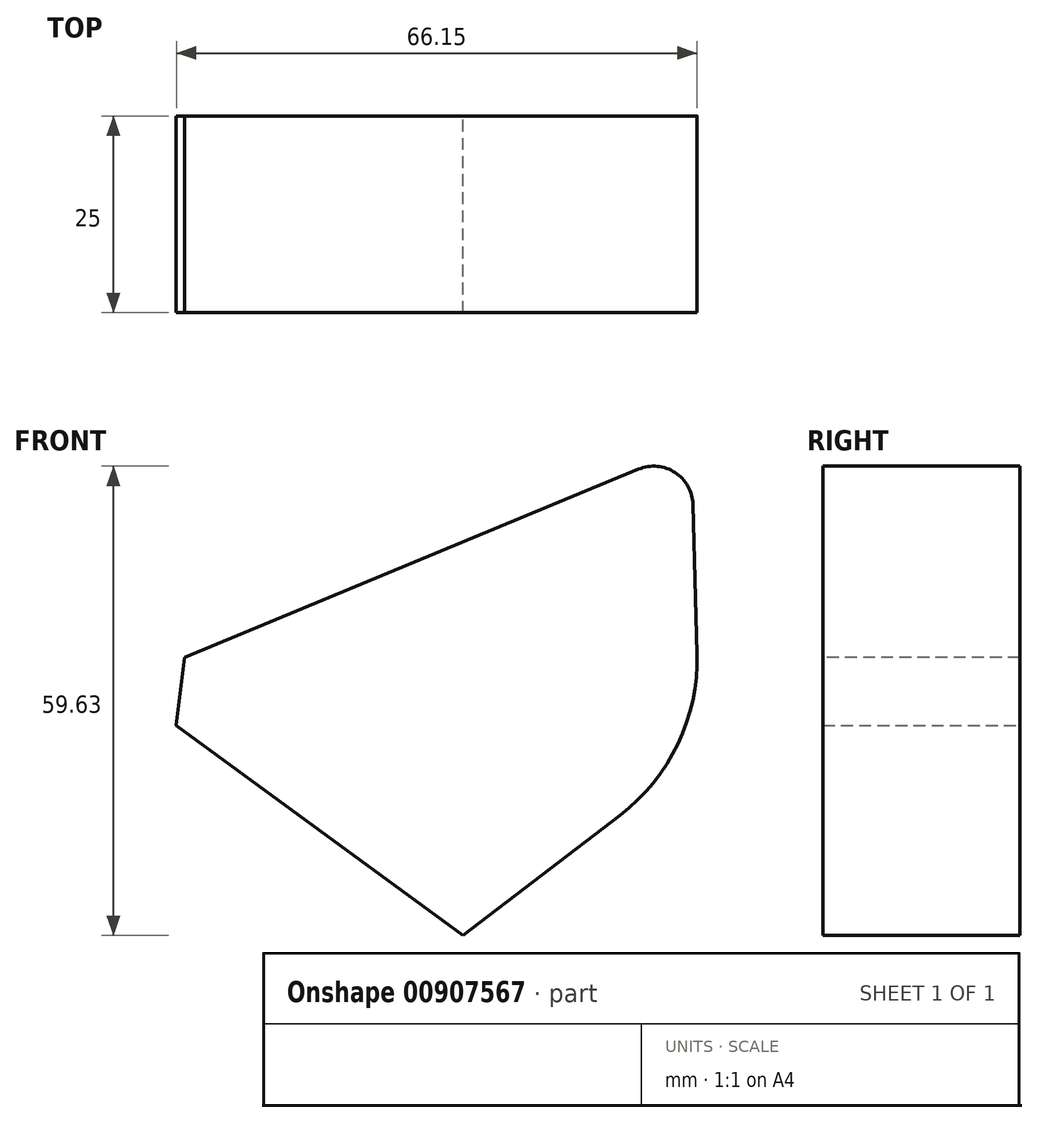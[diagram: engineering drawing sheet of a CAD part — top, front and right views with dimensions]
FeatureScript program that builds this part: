
annotation { "Feature Type Name" : "Feature", "Feature Type Description" : "" }
export const myFeature = defineFeature(function(context is Context, id is Id, definition is map)
    precondition{}
    {
        {
            var Q0;
            Q0=qCreatedBy(makeId("Front.planeOp"),FACE);
            var sketch = newSketch(context, id + "F0", { "sketchPlane" : qUnion([Q0])});
            skLineSegment(sketch, "E0", {"start": v(30.08, 23.03) * mm, "end": v(0, 0) * mm});
            skLineSegment(sketch, "E1", {"start": v(0, 0) * mm, "end": v(-43.57, 31.95) * mm});
            skLineSegment(sketch, "E2", {"start": v(-43.57, 31.95) * mm, "end": v(29.04, 62.03) * mm});
            skLineSegment(sketch, "E3", {"start": v(29.04, 62.03) * mm, "end": v(30.08, 23.03) * mm});
            skSolve(sketch);
        }
        {
            var Q0;
            Q0=makeQuery(id+"F0.imprint","IMPRINT",FACE,{"disambiguationData":[TD([[makeQuery(id+"F0.imprint","IMPRINT",EDGE,{"derivedFrom":sQuery(id+"F0.wireOp",EDGE,"E0")}),-1.0]])]});
            extrude(context, id + "F1", {"entities" : qUnion([Q0]), "depth" : 25 * mm, "offsetDistance" : 25 * mm});
        }
        {
            var Q0;
            Q0=makeQuery(id+"F1.opExtrude","SWEPT_EDGE",EDGE,{"disambiguationData":[OSD([sQuery(id+"F0.wireOp",EDGE,"E1"),sQuery(id+"F0.wireOp",EDGE,"E2")])]});
            chamfer(context, id + "F2", {"entities" : qUnion([Q0]), "width" : 5 * mm, "tangentPropagation" : true});
        }
        {
            var Q0;
            Q0=makeQuery(id+"F1.opExtrude","SWEPT_EDGE",EDGE,{"disambiguationData":[OSD([sQuery(id+"F0.wireOp",EDGE,"E2"),sQuery(id+"F0.wireOp",EDGE,"E3")])]});
            fillet(context, id + "F3", {"entities" : qUnion([Q0]), "radius" : 5 * mm, "tangentPropagation" : true, "allowEdgeOverflow" : false});
        }
        {
            var Q0;
            Q0=makeQuery(id+"F1.opExtrude","SWEPT_EDGE",EDGE,{"disambiguationData":[OSD([sQuery(id+"F0.wireOp",EDGE,"E0"),sQuery(id+"F0.wireOp",EDGE,"E3")])]});
            fillet(context, id + "F4", {"entities" : qUnion([Q0]), "radius" : 25 * mm, "tangentPropagation" : true, "allowEdgeOverflow" : false});
        }
        {
            var Q0;
            Q0=makeQuery(id+"F1.opExtrude","CAP_FACE",FACE,{"disambiguationData":[OSD([sQuery(id+"F0.wireOp",EDGE,"E0"),sQuery(id+"F0.wireOp",EDGE,"E1"),sQuery(id+"F0.wireOp",EDGE,"E2"),sQuery(id+"F0.wireOp",EDGE,"E3")])],"isStart":false});
            var sketch = newSketch(context, id + "F5", { "sketchPlane" : qUnion([Q0])});
            skCircle(sketch, "E4", {"center": v(0, 40.23) * mm, "radius": 7.05 * mm});
            skSolve(sketch);
        }
        {
            var Q0;
            Q0 = qSketchRegion(id + "F5", true);
            extrude(context, id + "F6", {"entities" : qUnion([Q0]), "operationType" : NewBodyOperationType.ADD, "oppositeDirection" : true, "depth" : 25 * mm, "offsetDistance" : 25 * mm});
        }
    });
